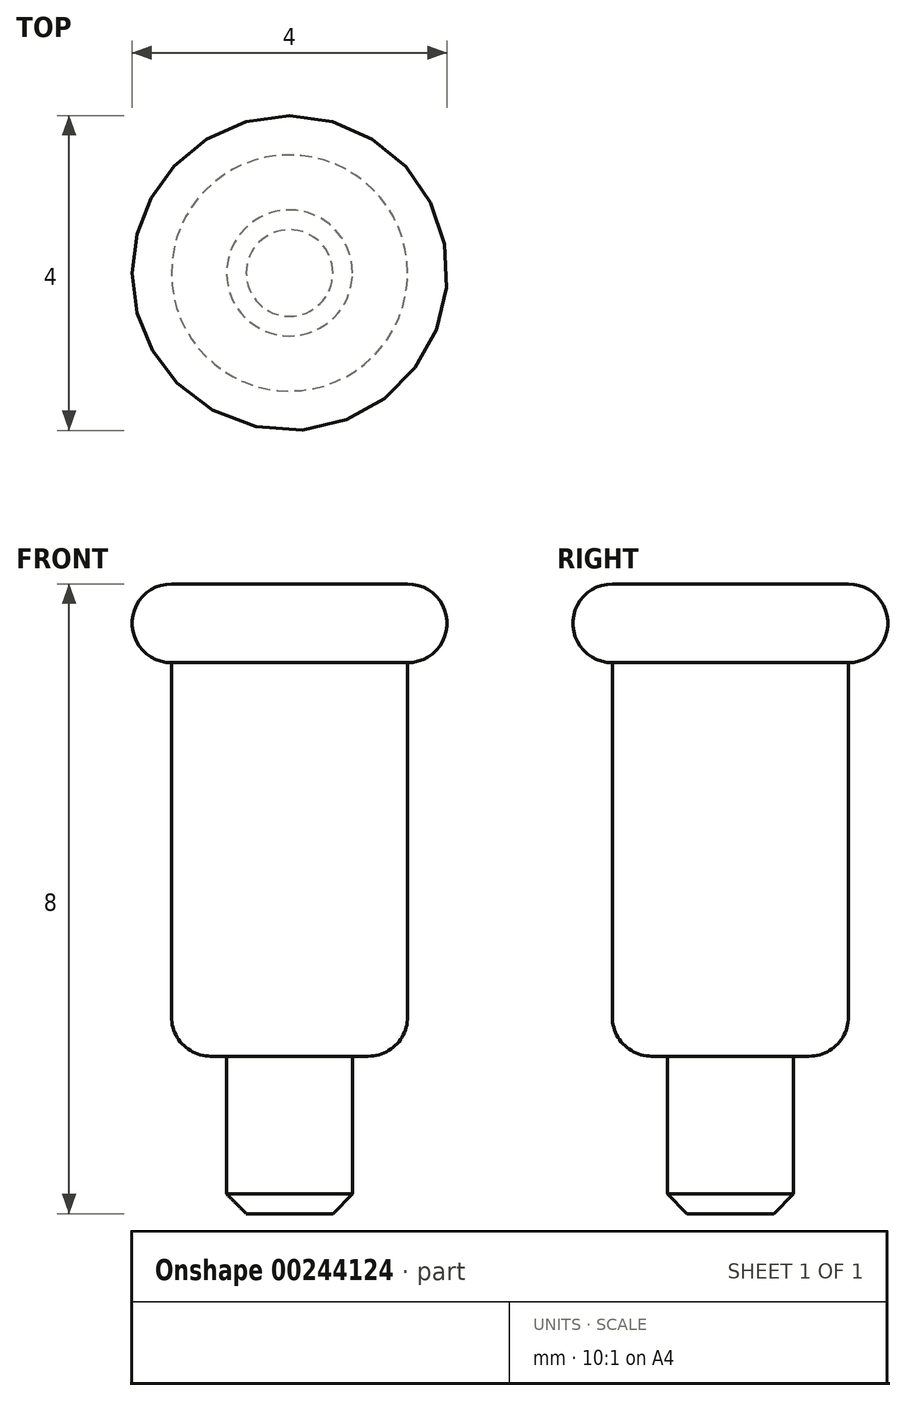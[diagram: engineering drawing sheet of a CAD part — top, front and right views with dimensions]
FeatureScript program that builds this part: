
annotation { "Feature Type Name" : "Feature", "Feature Type Description" : "" }
export const myFeature = defineFeature(function(context is Context, id is Id, definition is map)
    precondition{}
    {
        {
            var Q0;
            Q0=qCreatedBy(makeId("Front.planeOp"),FACE);
            var sketch = newSketch(context, id + "F0", { "sketchPlane" : qUnion([Q0])});
            skLineSegment(sketch, "E0", {"start": v(0, 0) * mm, "end": v(0.8, 0) * mm});
            skLineSegment(sketch, "E1", {"start": v(0.8, 2) * mm, "end": v(1.5, 2) * mm});
            skLineSegment(sketch, "E2", {"start": v(1.5, 7) * mm, "end": v(2, 7) * mm});
            skLineSegment(sketch, "E3", {"start": v(0, 0) * mm, "end": v(0, 8) * mm});
            skLineSegment(sketch, "E4", {"start": v(0, 8) * mm, "end": v(2, 8) * mm});
            skLineSegment(sketch, "E5", {"start": v(0.8, 0) * mm, "end": v(0.8, 2) * mm});
            skLineSegment(sketch, "E6", {"start": v(1.5, 2) * mm, "end": v(1.5, 7) * mm});
            skLineSegment(sketch, "E7.trimOffspring", {"start": v(2, 7) * mm, "end": v(2, 8) * mm});
            skSolve(sketch);
        }
        {
            var Q0;
            Q0=makeQuery(id+"F0.imprint","IMPRINT",FACE,{"disambiguationData":[TD([[makeQuery(id+"F0.imprint","IMPRINT",EDGE,{"derivedFrom":sQuery(id+"F0.wireOp",EDGE,"E1")}),1.0]])]});
            var Q1;
            Q1=sQuery(id+"F0.wireOp",EDGE,"E3");
            revolve(context, id + "F1", {"entities" : qUnion([Q0]), "axis" : qUnion([Q1]), "revolveType" : RevolveType.FULL});
        }
        {
            var Q0;
            Q0=makeQuery(id+"F1.opRevolve","SWEPT_FACE",FACE,{"disambiguationData":[OSD([sQuery(id+"F0.wireOp",EDGE,"E7.trimOffspring")])]});
            var Q1;
            Q1=makeQuery(id+"F1.opRevolve","SWEPT_EDGE",EDGE,{"disambiguationData":[OSD([sQuery(id+"F0.wireOp",EDGE,"E1"),sQuery(id+"F0.wireOp",EDGE,"E6")])]});
            fillet(context, id + "F2", {"entities" : qUnion([Q0, Q1]), "radius" : .5 * mm, "tangentPropagation" : true, "allowEdgeOverflow" : false});
        }
        {
            var Q0;
            Q0=makeQuery(id+"F1.opRevolve","SWEPT_EDGE",EDGE,{"disambiguationData":[OSD([sQuery(id+"F0.wireOp",EDGE,"E0"),sQuery(id+"F0.wireOp",EDGE,"E5")])]});
            chamfer(context, id + "F3", {"entities" : qUnion([Q0]), "chamferType" : ChamferType.OFFSET_ANGLE, "width" : .25 * mm, "oppositeDirection" : false, "angle" : 45 * degree, "tangentPropagation" : true});
        }
    });
